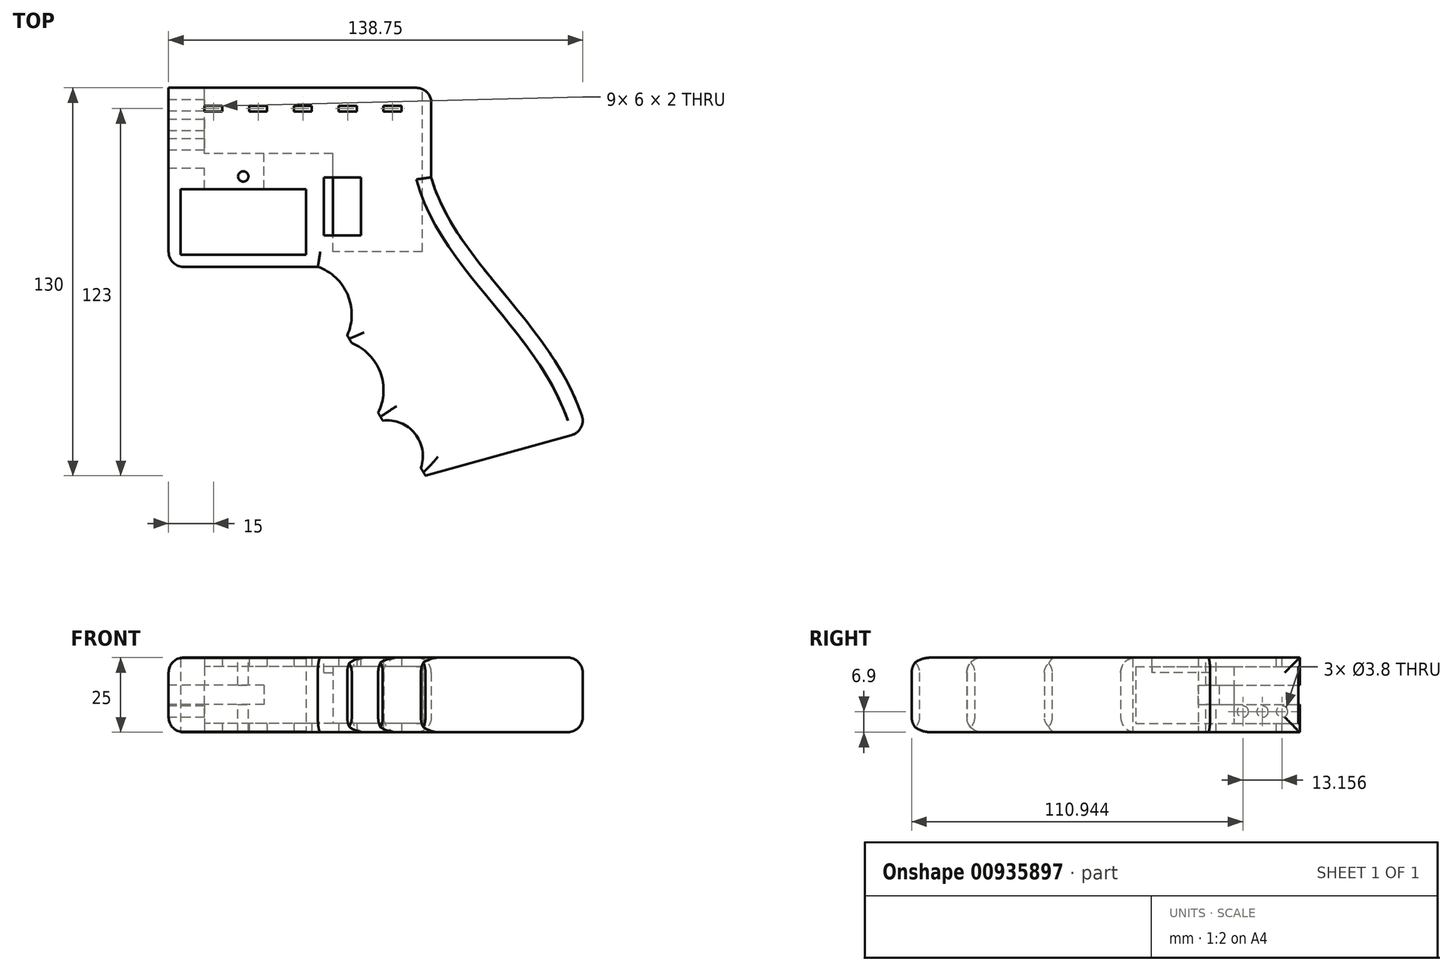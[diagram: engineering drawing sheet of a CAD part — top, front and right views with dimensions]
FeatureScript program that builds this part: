
annotation { "Feature Type Name" : "Feature", "Feature Type Description" : "" }
export const myFeature = defineFeature(function(context is Context, id is Id, definition is map)
    precondition{}
    {
        {
            var Q0;
            Q0=qCreatedBy(makeId("Top.planeOp"),FACE);
            var sketch = newSketch(context, id + "F0", { "sketchPlane" : qUnion([Q0])});
            skLineSegment(sketch, "E0.bottom", {"start": v(44, -30) * mm, "end": v(-44, -30) * mm});
            skLineSegment(sketch, "E0.top", {"start": v(44, 30) * mm, "end": v(-44, 30) * mm});
            skLineSegment(sketch, "E0.left", {"start": v(44, -30) * mm, "end": v(44, 30) * mm});
            skLineSegment(sketch, "E0.right", {"start": v(-44, -30) * mm, "end": v(-44, 30) * mm});
            skPoint(sketch, "E0.middle", {"position": v(0, 0) * mm});
            skLineSegment(sketch, "E1.bottom", {"start": v(-40, -4) * mm, "end": v(2, -4) * mm});
            skLineSegment(sketch, "E1.top", {"start": v(-40, -26) * mm, "end": v(2, -26) * mm});
            skLineSegment(sketch, "E1.left", {"start": v(-40, -4) * mm, "end": v(-40, -26) * mm});
            skLineSegment(sketch, "E1.right", {"start": v(2, -4) * mm, "end": v(2, -26) * mm});
            skLineSegment(sketch, "E2.bottom", {"start": v(-32, 24) * mm, "end": v(-26, 24) * mm});
            skLineSegment(sketch, "E2.top", {"start": v(-32, 22) * mm, "end": v(-26, 22) * mm});
            skLineSegment(sketch, "E2.left", {"start": v(-32, 24) * mm, "end": v(-32, 22) * mm});
            skLineSegment(sketch, "E2.right", {"start": v(-26, 24) * mm, "end": v(-26, 22) * mm});
            skFitSpline(sketch, "E3", {"points": [v(44, 0) * mm, v(96, -85) * mm], "startDerivative": vector(25.3, -90.03) * mm, "endDerivative": vector(26.88, -103.96) * mm});
            skLineSegment(sketch, "E4.1.0.0", {"start": v(-11, 24) * mm, "end": v(-11, 22) * mm});
            skLineSegment(sketch, "E4.1.0.1", {"start": v(-17, 22) * mm, "end": v(-11, 22) * mm});
            skLineSegment(sketch, "E4.1.0.2", {"start": v(-17, 24) * mm, "end": v(-17, 22) * mm});
            skLineSegment(sketch, "E4.1.0.3", {"start": v(-17, 24) * mm, "end": v(-11, 24) * mm});
            skLineSegment(sketch, "E4.2.0.0", {"start": v(4, 24) * mm, "end": v(4, 22) * mm});
            skLineSegment(sketch, "E4.2.0.1", {"start": v(-2, 22) * mm, "end": v(4, 22) * mm});
            skLineSegment(sketch, "E4.2.0.2", {"start": v(-2, 24) * mm, "end": v(-2, 22) * mm});
            skLineSegment(sketch, "E4.2.0.3", {"start": v(-2, 24) * mm, "end": v(4, 24) * mm});
            skLineSegment(sketch, "E4.direction1", {"start": v(-26, 22) * mm, "end": v(-11, 22) * mm, "construction": true});
            skLineSegment(sketch, "E5.0.3.0", {"start": v(19, 24) * mm, "end": v(19, 22) * mm});
            skLineSegment(sketch, "E5.3.3.0", {"start": v(13, 22) * mm, "end": v(19, 22) * mm});
            skLineSegment(sketch, "E5.6.3.0", {"start": v(13, 24) * mm, "end": v(13, 22) * mm});
            skLineSegment(sketch, "E5.9.3.0", {"start": v(13, 24) * mm, "end": v(19, 24) * mm});
            skLineSegment(sketch, "E5.0.4.0", {"start": v(34, 24) * mm, "end": v(34, 22) * mm});
            skLineSegment(sketch, "E5.3.4.0", {"start": v(28, 22) * mm, "end": v(34, 22) * mm});
            skLineSegment(sketch, "E5.6.4.0", {"start": v(28, 24) * mm, "end": v(28, 22) * mm});
            skLineSegment(sketch, "E5.9.4.0", {"start": v(28, 24) * mm, "end": v(34, 24) * mm});
            skLineSegment(sketch, "E6", {"start": v(96, -85) * mm, "end": v(42.05, -100) * mm});
            skLineSegment(sketch, "E7", {"start": v(42.05, -100) * mm, "end": v(40.52, -97.42) * mm});
            skArc(sketch, "E8", {"start": v(40.52, -97.42) * mm, "mid": v(38.55, -85.92) * mm, "end": v(27.74, -81.53) * mm});
            skLineSegment(sketch, "E9", {"start": v(27.74, -81.53) * mm, "end": v(26.22, -78.95) * mm});
            skArc(sketch, "E10", {"start": v(26.22, -78.95) * mm, "mid": v(26.92, -65.32) * mm, "end": v(17.37, -55.56) * mm});
            skLineSegment(sketch, "E11", {"start": v(17.37, -55.56) * mm, "end": v(15.84, -52.98) * mm});
            skArc(sketch, "E12", {"start": v(15.84, -52.98) * mm, "mid": v(15.96, -39.33) * mm, "end": v(6, -30) * mm});
            skSolve(sketch);
        }
        {
            var Q0;
            {var subQ0=sQuery(id+"F0.wireOp",EDGE,"E3");Q0=makeQuery(id+"F0.imprint","IMPRINT",FACE,{"disambiguationData":[TD([[makeQuery(id+"F0.imprint","IMPRINT",EDGE,{"derivedFrom":subQ0}),-1.0]])]});}
            var Q1;
            {var subQ4=sQuery(id+"F0.wireOp",EDGE,"E0.top");Q1=makeQuery(id+"F0.imprint","IMPRINT",FACE,{"disambiguationData":[TD([[makeQuery(id+"F0.imprint","IMPRINT",EDGE,{"derivedFrom":subQ4}),1.0]])]});}
            extrude(context, id + "F1", {"entities" : qUnion([Q0, Q1]), "depth" : 25 * mm, "offsetDistance" : 25 * mm});
        }
        {
            var Q0;
            Q0=makeQuery(id+"F1.opExtrude","SWEPT_FACE",FACE,{"disambiguationData":[OSD([sQuery(id+"F0.wireOp",EDGE,"E0.top")])]});
            var sketch = newSketch(context, id + "F2", { "sketchPlane" : qUnion([Q0])});
            skLineSegment(sketch, "E13.bottom", {"start": v(0, 0) * mm, "end": v(0, 0) * mm});
            skLineSegment(sketch, "E13.top", {"start": v(0, 25) * mm, "end": v(0, 25) * mm});
            skLineSegment(sketch, "E13.left", {"start": v(0, 0) * mm, "end": v(0, 25) * mm});
            skLineSegment(sketch, "E13.right", {"start": v(0, 0) * mm, "end": v(0, 25) * mm});
            skLineSegment(sketch, "E14.bottom", {"start": v(-41, 22) * mm, "end": v(32, 22) * mm});
            skLineSegment(sketch, "E14.top", {"start": v(-41, 3) * mm, "end": v(32, 3) * mm});
            skLineSegment(sketch, "E14.left", {"start": v(-41, 22) * mm, "end": v(-41, 3) * mm});
            skLineSegment(sketch, "E14.right", {"start": v(32, 22) * mm, "end": v(32, 3) * mm});
            skLineSegment(sketch, "E15", {"start": v(-11, 22) * mm, "end": v(-11, 3) * mm});
            skPoint(sketch, "E15.endSnap0", {"position": v(-4.5, 3) * mm});
            skLineSegment(sketch, "E16.right", {"start": v(32, 15.75) * mm, "end": v(32, 9.25) * mm});
            skLineSegment(sketch, "E17.bottom", {"start": v(12, 15.75) * mm, "end": v(44, 15.75) * mm});
            skLineSegment(sketch, "E17.top", {"start": v(12, 9.25) * mm, "end": v(44, 9.25) * mm});
            skLineSegment(sketch, "E17.left", {"start": v(12, 15.75) * mm, "end": v(12, 9.25) * mm});
            skLineSegment(sketch, "E17.right", {"start": v(44, 15.75) * mm, "end": v(44, 9.25) * mm});
            skLineSegment(sketch, "E18", {"start": v(21.68, 22) * mm, "end": v(21.68, 15.75) * mm, "construction": true});
            skLineSegment(sketch, "E19", {"start": v(21.68, 9.25) * mm, "end": v(21.68, 3) * mm});
            skSolve(sketch);
        }
        {
            var Q0;
            {var subQ10=sQuery(id+"F2.wireOp",EDGE,"E17.left");Q0=makeQuery(id+"F2.imprint","IMPRINT",FACE,{"disambiguationData":[TD([[makeQuery(id+"F2.imprint","IMPRINT",EDGE,{"derivedFrom":subQ10}),-1.0]])]});}
            var Q1;
            {var subQ5=sQuery(id+"F2.wireOp",EDGE,"E15");Q1=makeQuery(id+"F2.imprint","IMPRINT",FACE,{"disambiguationData":[TD([[makeQuery(id+"F2.imprint","IMPRINT",EDGE,{"derivedFrom":subQ5}),1.0]])]});}
            var Q2;
            {var subQ2=sQuery(id+"F2.wireOp",EDGE,"E17.left");Q2=makeQuery(id+"F2.imprint","IMPRINT",FACE,{"disambiguationData":[TD([[makeQuery(id+"F2.imprint","IMPRINT",EDGE,{"derivedFrom":subQ2}),1.0]])]});}
            var Q3;
            {var subQ3=sQuery(id+"F2.wireOp",EDGE,"E19");Q3=makeQuery(id+"F2.imprint","IMPRINT",FACE,{"disambiguationData":[TD([[makeQuery(id+"F2.imprint","IMPRINT",EDGE,{"derivedFrom":subQ3}),1.0]])]});}
            var Q4;
            {var subQ5=sQuery(id+"F2.wireOp",EDGE,"E17.right");Q4=makeQuery(id+"F2.imprint","IMPRINT",FACE,{"disambiguationData":[TD([[makeQuery(id+"F2.imprint","IMPRINT",EDGE,{"derivedFrom":subQ5}),-1.0]])]});}
            var Q5;
            {var subQ0=sQuery(id+"F2.wireOp",EDGE,"E14.left");Q5=makeQuery(id+"F2.imprint","IMPRINT",FACE,{"disambiguationData":[TD([[makeQuery(id+"F2.imprint","IMPRINT",EDGE,{"derivedFrom":subQ0}),1.0]])]});}
            extrude(context, id + "F3", {"entities" : qUnion([Q0, Q1, Q2, Q3, Q4, Q5]), "operationType" : NewBodyOperationType.REMOVE, "oppositeDirection" : true, "depth" : 22 * mm, "offsetDistance" : 25 * mm});
        }
        {
            var Q0;
            {var subQ0=sQuery(id+"F2.wireOp",EDGE,"E14.left");Q0=makeQuery(id+"F2.imprint","IMPRINT",FACE,{"disambiguationData":[TD([[makeQuery(id+"F2.imprint","IMPRINT",EDGE,{"derivedFrom":subQ0}),1.0]])]});}
            extrude(context, id + "F4", {"entities" : qUnion([Q0]), "operationType" : NewBodyOperationType.REMOVE, "oppositeDirection" : true, "depth" : 55 * mm, "offsetDistance" : 25 * mm});
        }
        {
            var Q0;
            {var subQ2=sQuery(id+"F2.wireOp",EDGE,"E17.left");Q0=makeQuery(id+"F2.imprint","IMPRINT",FACE,{"disambiguationData":[TD([[makeQuery(id+"F2.imprint","IMPRINT",EDGE,{"derivedFrom":subQ2}),1.0]])]});}
            var Q1;
            Q1=makeQuery(id+"F1.opExtrude","SWEPT_FACE",FACE,{"disambiguationData":[OSD([sQuery(id+"F0.wireOp",EDGE,"E1.bottom")])]});
            extrude(context, id + "F5", {"entities" : qUnion([Q0]), "operationType" : NewBodyOperationType.REMOVE, "endBound" : BoundingType.UP_TO_SURFACE, "oppositeDirection" : true, "depth" : 25 * mm, "endBoundEntityFace" : qUnion([Q1]), "offsetDistance" : 25 * mm});
        }
        {
            var Q0;
            {var subQ5=sQuery(id+"F2.wireOp",EDGE,"E17.right");Q0=makeQuery(id+"F2.imprint","IMPRINT",FACE,{"disambiguationData":[TD([[makeQuery(id+"F2.imprint","IMPRINT",EDGE,{"derivedFrom":subQ5}),-1.0]])]});}
            extrude(context, id + "F6", {"entities" : qUnion([Q0]), "operationType" : NewBodyOperationType.REMOVE, "oppositeDirection" : true, "depth" : 27 * mm, "offsetDistance" : 25 * mm});
        }
        {
            var Q0;
            Q0=makeQuery(id+"F1.opExtrude","CAP_FACE",FACE,{"disambiguationData":[OSD([sQuery(id+"F0.wireOp",EDGE,"E0.bottom"),sQuery(id+"F0.wireOp",EDGE,"E0.top"),sQuery(id+"F0.wireOp",EDGE,"E0.left"),sQuery(id+"F0.wireOp",EDGE,"E0.right"),sQuery(id+"F0.wireOp",EDGE,"E1.bottom"),sQuery(id+"F0.wireOp",EDGE,"E1.top"),sQuery(id+"F0.wireOp",EDGE,"E1.left"),sQuery(id+"F0.wireOp",EDGE,"E1.right"),sQuery(id+"F0.wireOp",EDGE,"E2.bottom"),sQuery(id+"F0.wireOp",EDGE,"E2.top"),sQuery(id+"F0.wireOp",EDGE,"E2.left"),sQuery(id+"F0.wireOp",EDGE,"E2.right"),sQuery(id+"F0.wireOp",EDGE,"E3"),sQuery(id+"F0.wireOp",EDGE,"E4.1.0.0"),sQuery(id+"F0.wireOp",EDGE,"E4.1.0.1"),sQuery(id+"F0.wireOp",EDGE,"E4.1.0.2"),sQuery(id+"F0.wireOp",EDGE,"E4.1.0.3"),sQuery(id+"F0.wireOp",EDGE,"E4.2.0.0"),sQuery(id+"F0.wireOp",EDGE,"E4.2.0.1"),sQuery(id+"F0.wireOp",EDGE,"E4.2.0.2"),sQuery(id+"F0.wireOp",EDGE,"E4.2.0.3"),sQuery(id+"F0.wireOp",EDGE,"E5.0.3.0"),sQuery(id+"F0.wireOp",EDGE,"E5.3.3.0"),sQuery(id+"F0.wireOp",EDGE,"E5.6.3.0"),sQuery(id+"F0.wireOp",EDGE,"E5.9.3.0"),sQuery(id+"F0.wireOp",EDGE,"E5.0.4.0"),sQuery(id+"F0.wireOp",EDGE,"E5.3.4.0"),sQuery(id+"F0.wireOp",EDGE,"E5.6.4.0"),sQuery(id+"F0.wireOp",EDGE,"E5.9.4.0"),sQuery(id+"F0.wireOp",EDGE,"E6"),sQuery(id+"F0.wireOp",EDGE,"E7"),sQuery(id+"F0.wireOp",EDGE,"E8"),sQuery(id+"F0.wireOp",EDGE,"E9"),sQuery(id+"F0.wireOp",EDGE,"E10"),sQuery(id+"F0.wireOp",EDGE,"E11"),sQuery(id+"F0.wireOp",EDGE,"E12")])],"isStart":false});
            var sketch = newSketch(context, id + "F7", { "sketchPlane" : qUnion([Q0])});
            skCircle(sketch, "E20", {"center": v(-19, 0.3) * mm, "radius": 1.75 * mm});
            skPoint(sketch, "E20.centerSnap0", {"position": v(-19, -4) * mm});
            skSolve(sketch);
        }
        {
            var Q0;
            Q0=makeQuery(id+"F7.imprint","IMPRINT",FACE,{"disambiguationData":[TD([[makeQuery(id+"F7.imprint","IMPRINT",EDGE,{"derivedFrom":sQuery(id+"F7.wireOp",EDGE,"E20")}),1.0]])]});
            extrude(context, id + "F8", {"entities" : qUnion([Q0]), "operationType" : NewBodyOperationType.REMOVE, "endBound" : BoundingType.THROUGH_ALL, "oppositeDirection" : true, "depth" : 25 * mm, "offsetDistance" : 25 * mm});
        }
        {
            var Q0;
            Q0=makeQuery(id+"F1.opExtrude","CAP_EDGE",EDGE,{"disambiguationData":[OSD([sQuery(id+"F0.wireOp",EDGE,"E8")])],"isStart":false});
            var Q1;
            Q1=makeQuery(id+"F1.opExtrude","CAP_EDGE",EDGE,{"disambiguationData":[OSD([sQuery(id+"F0.wireOp",EDGE,"E10")])],"isStart":false});
            var Q2;
            Q2=makeQuery(id+"F1.opExtrude","CAP_EDGE",EDGE,{"disambiguationData":[OSD([sQuery(id+"F0.wireOp",EDGE,"E12")])],"isStart":false});
            var Q3;
            Q3=makeQuery(id+"F1.opExtrude","CAP_EDGE",EDGE,{"disambiguationData":[OSD([sQuery(id+"F0.wireOp",EDGE,"E12")])],"isStart":true});
            var Q4;
            Q4=makeQuery(id+"F1.opExtrude","CAP_EDGE",EDGE,{"disambiguationData":[OSD([sQuery(id+"F0.wireOp",EDGE,"E10")])],"isStart":true});
            var Q5;
            Q5=makeQuery(id+"F1.opExtrude","CAP_EDGE",EDGE,{"disambiguationData":[OSD([sQuery(id+"F0.wireOp",EDGE,"E8")])],"isStart":true});
            var Q6;
            Q6=makeQuery(id+"F1.opExtrude","CAP_EDGE",EDGE,{"disambiguationData":[OSD([sQuery(id+"F0.wireOp",EDGE,"E0.bottom")])],"isStart":false});
            var Q7;
            Q7=makeQuery(id+"F1.opExtrude","CAP_EDGE",EDGE,{"disambiguationData":[OSD([sQuery(id+"F0.wireOp",EDGE,"E0.bottom")])],"isStart":true});
            var Q8;
            Q8=makeQuery(id+"F1.opExtrude","CAP_EDGE",EDGE,{"disambiguationData":[OSD([sQuery(id+"F0.wireOp",EDGE,"E0.right")])],"isStart":true});
            var Q9;
            Q9=makeQuery(id+"F1.opExtrude","CAP_EDGE",EDGE,{"disambiguationData":[OSD([sQuery(id+"F0.wireOp",EDGE,"E0.right")])],"isStart":false});
            var Q10;
            Q10=makeQuery(id+"F1.opExtrude","CAP_EDGE",EDGE,{"disambiguationData":[OSD([sQuery(id+"F0.wireOp",EDGE,"E3")])],"isStart":true});
            var Q11;
            Q11=makeQuery(id+"F1.opExtrude","CAP_EDGE",EDGE,{"disambiguationData":[OSD([sQuery(id+"F0.wireOp",EDGE,"E3")])],"isStart":false});
            var Q12;
            Q12=makeQuery(id+"F1.opExtrude","SWEPT_EDGE",EDGE,{"disambiguationData":[OSD([sQuery(id+"F0.wireOp",EDGE,"E3"),sQuery(id+"F0.wireOp",EDGE,"E6")])]});
            var Q13;
            Q13=makeQuery(id+"F1.opExtrude","CAP_EDGE",EDGE,{"disambiguationData":[OSD([sQuery(id+"F0.wireOp",EDGE,"E6")])],"isStart":false});
            var Q14;
            Q14=makeQuery(id+"F1.opExtrude","CAP_EDGE",EDGE,{"disambiguationData":[OSD([sQuery(id+"F0.wireOp",EDGE,"E6")])],"isStart":true});
            var Q15;
            Q15=makeQuery(id+"F1.opExtrude","CAP_EDGE",EDGE,{"disambiguationData":[OSD([sQuery(id+"F0.wireOp",EDGE,"E0.left")])],"isStart":true});
            var Q16;
            Q16=makeQuery(id+"F1.opExtrude","CAP_EDGE",EDGE,{"disambiguationData":[OSD([sQuery(id+"F0.wireOp",EDGE,"E0.left")])],"isStart":false});
            var Q17;
            Q17=makeQuery(id+"F1.opExtrude","SWEPT_EDGE",EDGE,{"disambiguationData":[OSD([sQuery(id+"F0.wireOp",EDGE,"E0.top"),sQuery(id+"F0.wireOp",EDGE,"E0.left")])]});
            fillet(context, id + "F9", {"entities" : qUnion([Q0, Q1, Q2, Q3, Q4, Q5, Q6, Q7, Q8, Q9, Q10, Q11, Q12, Q13, Q14, Q15, Q16, Q17]), "radius" : 5 * mm, "tangentPropagation" : true, "allowEdgeOverflow" : false});
        }
        {
            var Q0;
            Q0=makeQuery(id+"F1.opExtrude","SWEPT_EDGE",EDGE,{"disambiguationData":[OSD([sQuery(id+"F0.wireOp",EDGE,"E0.bottom"),sQuery(id+"F0.wireOp",EDGE,"E0.right")])]});
            fillet(context, id + "F10", {"entities" : qUnion([Q0]), "radius" : 5 * mm, "tangentPropagation" : true, "allowEdgeOverflow" : false});
        }
        {
            var Q0;
            Q0=makeQuery(id+"F1.opExtrude","CAP_FACE",FACE,{"disambiguationData":[OSD([sQuery(id+"F0.wireOp",EDGE,"E0.bottom"),sQuery(id+"F0.wireOp",EDGE,"E0.top"),sQuery(id+"F0.wireOp",EDGE,"E0.left"),sQuery(id+"F0.wireOp",EDGE,"E0.right"),sQuery(id+"F0.wireOp",EDGE,"E1.bottom"),sQuery(id+"F0.wireOp",EDGE,"E1.top"),sQuery(id+"F0.wireOp",EDGE,"E1.left"),sQuery(id+"F0.wireOp",EDGE,"E1.right"),sQuery(id+"F0.wireOp",EDGE,"E2.bottom"),sQuery(id+"F0.wireOp",EDGE,"E2.top"),sQuery(id+"F0.wireOp",EDGE,"E2.left"),sQuery(id+"F0.wireOp",EDGE,"E2.right"),sQuery(id+"F0.wireOp",EDGE,"E3"),sQuery(id+"F0.wireOp",EDGE,"E4.1.0.0"),sQuery(id+"F0.wireOp",EDGE,"E4.1.0.1"),sQuery(id+"F0.wireOp",EDGE,"E4.1.0.2"),sQuery(id+"F0.wireOp",EDGE,"E4.1.0.3"),sQuery(id+"F0.wireOp",EDGE,"E4.2.0.0"),sQuery(id+"F0.wireOp",EDGE,"E4.2.0.1"),sQuery(id+"F0.wireOp",EDGE,"E4.2.0.2"),sQuery(id+"F0.wireOp",EDGE,"E4.2.0.3"),sQuery(id+"F0.wireOp",EDGE,"E5.0.3.0"),sQuery(id+"F0.wireOp",EDGE,"E5.3.3.0"),sQuery(id+"F0.wireOp",EDGE,"E5.6.3.0"),sQuery(id+"F0.wireOp",EDGE,"E5.9.3.0"),sQuery(id+"F0.wireOp",EDGE,"E5.0.4.0"),sQuery(id+"F0.wireOp",EDGE,"E5.3.4.0"),sQuery(id+"F0.wireOp",EDGE,"E5.6.4.0"),sQuery(id+"F0.wireOp",EDGE,"E5.9.4.0"),sQuery(id+"F0.wireOp",EDGE,"E6"),sQuery(id+"F0.wireOp",EDGE,"E7"),sQuery(id+"F0.wireOp",EDGE,"E8"),sQuery(id+"F0.wireOp",EDGE,"E9"),sQuery(id+"F0.wireOp",EDGE,"E10"),sQuery(id+"F0.wireOp",EDGE,"E11"),sQuery(id+"F0.wireOp",EDGE,"E12")])],"isStart":false});
            var sketch = newSketch(context, id + "F11", { "sketchPlane" : qUnion([Q0])});
            skLineSegment(sketch, "E21.bottom", {"start": v(8, 0) * mm, "end": v(20.5, 0) * mm});
            skLineSegment(sketch, "E21.top", {"start": v(8, -19.5) * mm, "end": v(20.5, -19.5) * mm});
            skLineSegment(sketch, "E21.left", {"start": v(8, 0) * mm, "end": v(8, -19.5) * mm});
            skLineSegment(sketch, "E21.right", {"start": v(20.5, 0) * mm, "end": v(20.5, -19.5) * mm});
            skSolve(sketch);
        }
        {
            var Q0;
            Q0=makeQuery(id+"F11.imprint","IMPRINT",FACE,{"disambiguationData":[TD([[makeQuery(id+"F11.imprint","IMPRINT",EDGE,{"derivedFrom":sQuery(id+"F11.wireOp",EDGE,"E21.bottom")}),-1.0]])]});
            extrude(context, id + "F12", {"entities" : qUnion([Q0]), "operationType" : NewBodyOperationType.REMOVE, "oppositeDirection" : true, "depth" : 5 * mm, "offsetDistance" : 25 * mm});
        }
        {
            var Q0;
            Q0=makeQuery(id+"F1.opExtrude","SWEPT_FACE",FACE,{"disambiguationData":[OSD([sQuery(id+"F0.wireOp",EDGE,"E0.right")])]});
            var sketch = newSketch(context, id + "F13", { "sketchPlane" : qUnion([Q0])});
            skCircle(sketch, "E22", {"center": v(-24.1, 6.9) * mm, "radius": 1.9 * mm});
            skCircle(sketch, "E23", {"center": v(-17.52, 6.9) * mm, "radius": 1.9 * mm});
            skCircle(sketch, "E24", {"center": v(-10.94, 6.9) * mm, "radius": 1.9 * mm});
            skSolve(sketch);
        }
        {
            var Q0;
            Q0=makeQuery(id+"F13.imprint","IMPRINT",FACE,{"disambiguationData":[TD([[makeQuery(id+"F13.imprint","IMPRINT",EDGE,{"derivedFrom":sQuery(id+"F13.wireOp",EDGE,"E22")}),1.0]])]});
            var Q1;
            Q1=makeQuery(id+"F13.imprint","IMPRINT",FACE,{"disambiguationData":[TD([[makeQuery(id+"F13.imprint","IMPRINT",EDGE,{"derivedFrom":sQuery(id+"F13.wireOp",EDGE,"E23")}),1.0]])]});
            var Q2;
            Q2=makeQuery(id+"F13.imprint","IMPRINT",FACE,{"disambiguationData":[TD([[makeQuery(id+"F13.imprint","IMPRINT",EDGE,{"derivedFrom":sQuery(id+"F13.wireOp",EDGE,"E24")}),1.0]])]});
            extrude(context, id + "F14", {"entities" : qUnion([Q0, Q1, Q2]), "operationType" : NewBodyOperationType.REMOVE, "oppositeDirection" : true, "depth" : 14 * mm, "offsetDistance" : 25 * mm});
        }
    });
